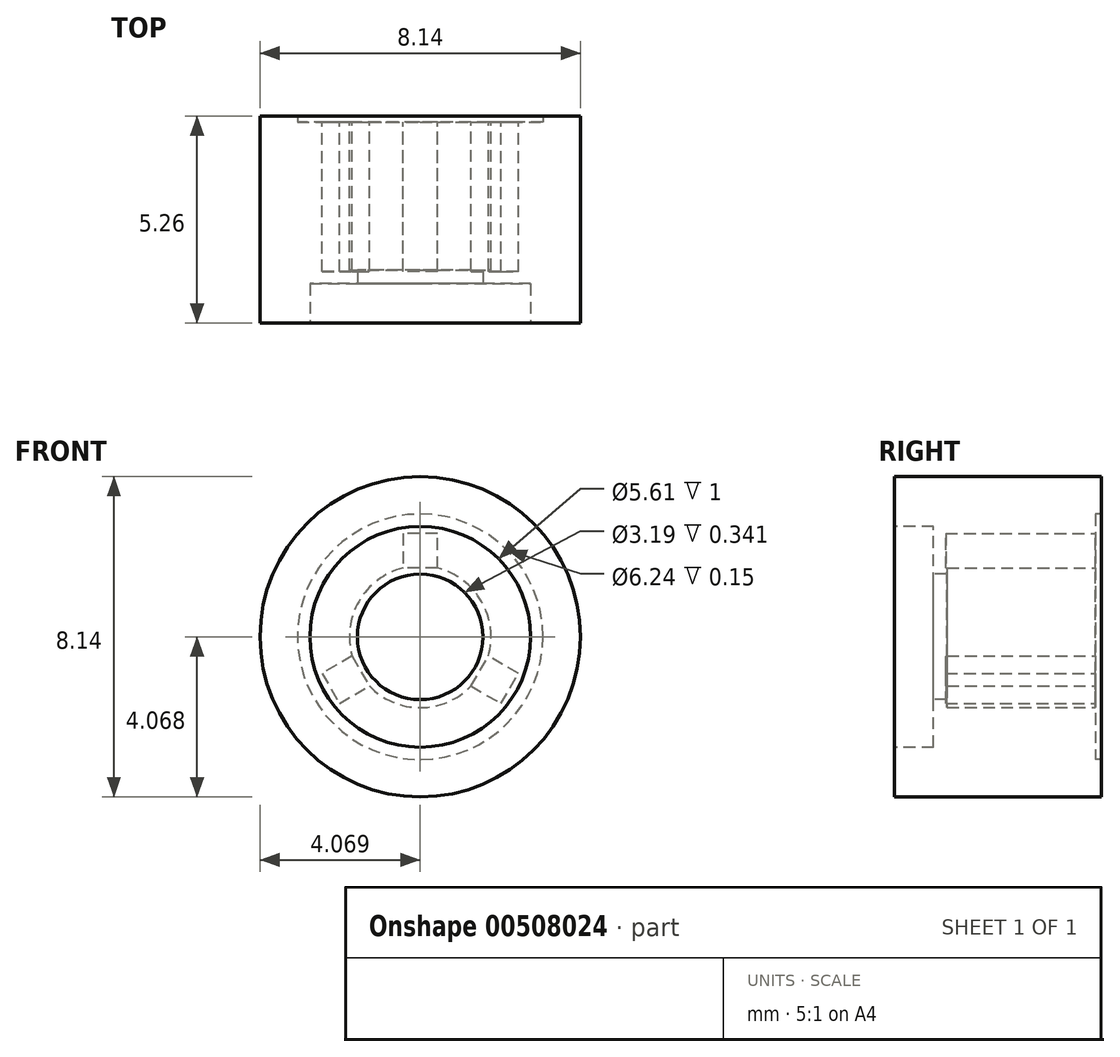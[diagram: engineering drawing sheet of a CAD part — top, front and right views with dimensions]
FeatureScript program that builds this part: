
annotation { "Feature Type Name" : "Feature", "Feature Type Description" : "" }
export const myFeature = defineFeature(function(context is Context, id is Id, definition is map)
    precondition{}
    {
        {
            var Q0;
            Q0=qCreatedBy(makeId("Front.planeOp"),FACE);
            var sketch = newSketch(context, id + "F0", { "sketchPlane" : qUnion([Q0])});
            skCircle(sketch, "E0", {"center": v(-37.22, 44.14) * mm, "radius": 4.07 * mm});
            skSolve(sketch);
        }
        {
            var Q0;
            Q0 = qSketchRegion(id + "F0", true);
            extrude(context, id + "F1", {"entities" : qUnion([Q0]), "depth" : 5.11 * mm, "offsetDistance" : 25 * mm});
        }
        {
            var Q0;
            Q0=makeQuery(id+"F1.opExtrude","CAP_FACE",FACE,{"disambiguationData":[OSD([sQuery(id+"F0.wireOp",EDGE,"E0")])],"isStart":false});
            var sketch = newSketch(context, id + "F2", { "sketchPlane" : qUnion([Q0])});
            skCircle(sketch, "E1", {"center": v(-37.22, 44.14) * mm, "radius": 2.8 * mm});
            skSolve(sketch);
        }
        {
            var Q0;
            Q0=makeQuery(id+"F2.imprint","IMPRINT",FACE,{"disambiguationData":[TD([[makeQuery(id+"F2.imprint","IMPRINT",EDGE,{"derivedFrom":sQuery(id+"F2.wireOp",EDGE,"E1")}),1.0]])]});
            extrude(context, id + "F3", {"entities" : qUnion([Q0]), "operationType" : NewBodyOperationType.REMOVE, "oppositeDirection" : true, "depth" : 1 * mm});
        }
        {
            var Q0;
            Q0=makeQuery(id+"F1.opExtrude","CAP_FACE",FACE,{"disambiguationData":[OSD([sQuery(id+"F0.wireOp",EDGE,"E0")])],"isStart":true});
            var sketch = newSketch(context, id + "F4", { "sketchPlane" : qUnion([Q0])});
            skCircle(sketch, "E2", {"center": v(37.22, 44.14) * mm, "radius": 1.8 * mm});
            skSolve(sketch);
        }
        {
            var Q0;
            Q0=makeQuery(id+"F4.imprint","IMPRINT",FACE,{"disambiguationData":[TD([[makeQuery(id+"F4.imprint","IMPRINT",EDGE,{"derivedFrom":sQuery(id+"F4.wireOp",EDGE,"E2")}),1.0]])]});
            extrude(context, id + "F5", {"entities" : qUnion([Q0]), "operationType" : NewBodyOperationType.REMOVE, "oppositeDirection" : true, "depth" : 3.77 * mm});
        }
        {
            var Q0;
            Q0=makeQuery(id+"F3.boolean.opBoolean","COPY",FACE,{"derivedFrom":makeQuery(id+"F3.opExtrude","CAP_FACE",FACE,{"disambiguationData":[OSD([sQuery(id+"F2.wireOp",EDGE,"E1")])],"isStart":false})});
            var sketch = newSketch(context, id + "F6", { "sketchPlane" : qUnion([Q0])});
            skCircle(sketch, "E3", {"center": v(-37.22, 44.14) * mm, "radius": 1.6 * mm});
            skSolve(sketch);
        }
        {
            var Q0;
            Q0 = qSketchRegion(id + "F6", true);
            extrude(context, id + "F7", {"entities" : qUnion([Q0]), "operationType" : NewBodyOperationType.REMOVE, "endBound" : BoundingType.THROUGH_ALL, "oppositeDirection" : true, "depth" : 25 * mm, "offsetDistance" : 25 * mm});
        }
        {
            var Q0;
            Q0=makeQuery(id+"F1.opExtrude","CAP_FACE",FACE,{"disambiguationData":[OSD([sQuery(id+"F0.wireOp",EDGE,"E0")])],"isStart":true});
            var sketch = newSketch(context, id + "F8", { "sketchPlane" : qUnion([Q0])});
            skLineSegment(sketch, "E4", {"start": v(36.78, 45.88) * mm, "end": v(36.78, 46.76) * mm});
            skLineSegment(sketch, "E5", {"start": v(37.66, 46.76) * mm, "end": v(37.66, 45.88) * mm});
            skLineSegment(sketch, "E6", {"start": v(36.78, 45.88) * mm, "end": v(37.66, 45.88) * mm});
            skLineSegment(sketch, "E7", {"start": v(36.78, 46.76) * mm, "end": v(37.66, 46.76) * mm});
            skLineSegment(sketch, "E8.1.0", {"start": v(35.17, 42.44) * mm, "end": v(34.73, 43.2) * mm});
            skLineSegment(sketch, "E8.1.1", {"start": v(35.93, 42.88) * mm, "end": v(35.49, 43.65) * mm});
            skLineSegment(sketch, "E8.1.2", {"start": v(35.93, 42.88) * mm, "end": v(35.17, 42.44) * mm});
            skLineSegment(sketch, "E8.1.3", {"start": v(34.73, 43.2) * mm, "end": v(35.49, 43.65) * mm});
            skLineSegment(sketch, "E8.2.0", {"start": v(39.72, 43.2) * mm, "end": v(39.28, 42.45) * mm});
            skLineSegment(sketch, "E8.2.1", {"start": v(38.95, 43.65) * mm, "end": v(38.51, 42.89) * mm});
            skLineSegment(sketch, "E8.2.2", {"start": v(38.95, 43.65) * mm, "end": v(39.72, 43.2) * mm});
            skLineSegment(sketch, "E8.2.3", {"start": v(39.28, 42.45) * mm, "end": v(38.51, 42.89) * mm});
            skPoint(sketch, "E8.center", {"position": v(37.22, 44.14) * mm});
            skSolve(sketch);
        }
        {
            var Q0;
            Q0 = qSketchRegion(id + "F8", true);
            extrude(context, id + "F9", {"entities" : qUnion([Q0]), "operationType" : NewBodyOperationType.REMOVE, "oppositeDirection" : true, "depth" : 3.8 * mm, "offsetDistance" : 25 * mm});
        }
        {
            var Q0;
            Q0=makeQuery(id+"F1.opExtrude","CAP_FACE",FACE,{"disambiguationData":[OSD([sQuery(id+"F0.wireOp",EDGE,"E0")])],"isStart":true});
            var sketch = newSketch(context, id + "F10", { "sketchPlane" : qUnion([Q0])});
            skCircle(sketch, "E9", {"center": v(37.22, 44.14) * mm, "radius": 4.07 * mm});
            skCircle(sketch, "E10", {"center": v(37.22, 44.14) * mm, "radius": 3.12 * mm});
            skSolve(sketch);
        }
        {
            var Q0;
            Q0 = qSketchRegion(id + "F10", true);
            extrude(context, id + "F11", {"entities" : qUnion([Q0]), "operationType" : NewBodyOperationType.ADD, "depth" : 0.15 * mm, "offsetDistance" : 25 * mm});
        }
    });
